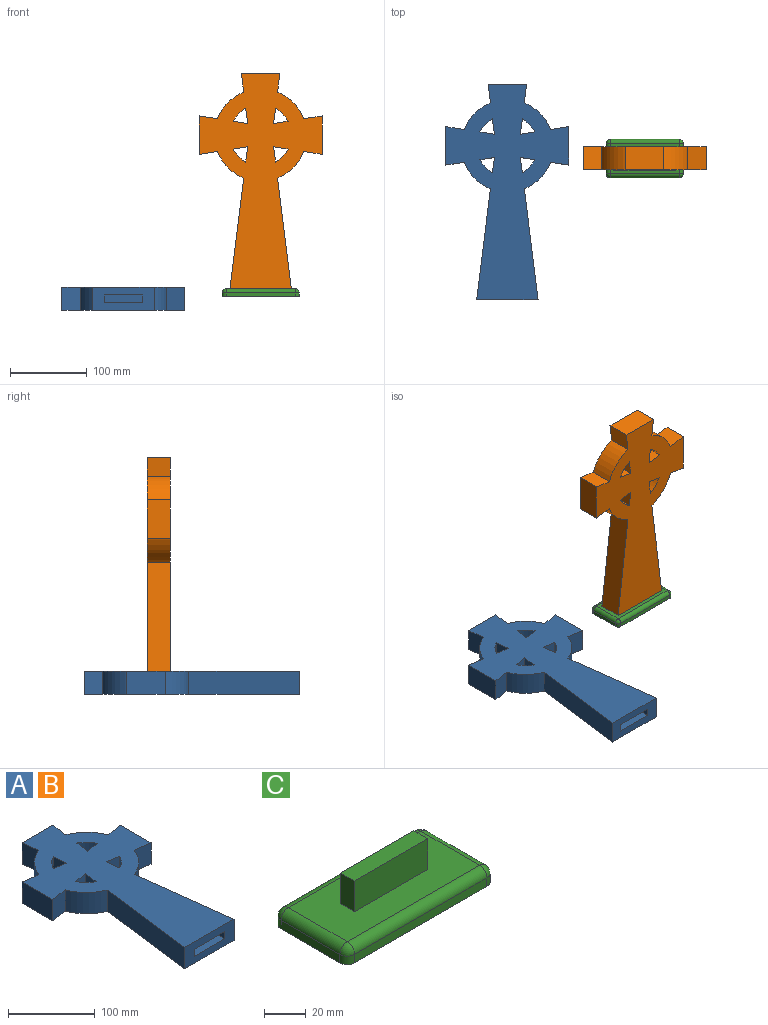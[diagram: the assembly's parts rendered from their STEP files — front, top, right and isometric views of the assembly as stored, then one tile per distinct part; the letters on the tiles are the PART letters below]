
ASSEMBLY  parts=3 mates=1
PART A: 35 faces, bbox 160x280x30 mm
  f0: plane 80x30mm, normal (0,-1,0), area 1900mm2, adj f15,f16,f28,f29,f30,f31,f32,f33
  f1: plane 30x18.79mm, normal (0.15,-0.99,0), area 570.6mm2, adj f2,f27,f28,f29
  f2: plane 30x19.86mm, normal (-0.99,0.12,0), area 600.3mm2, adj f1,f27,f28,f29
  f3: plane 30x19.86mm, normal (0.99,0.12,0), area 600.3mm2, adj f4,f23,f28,f29
  f4: plane 30x18.79mm, normal (-0.15,-0.99,0), area 570.6mm2, adj f3,f23,f28,f29
  f5: cylinder r=40mm len=30mm, axis (0,0,-1), area 715.5mm2, adj f6,f24,f28,f29
  f6: plane 30x19.86mm, normal (-0.99,-0.12,0), area 600.3mm2, adj f5,f24,f28,f29
  f7: plane 30x19.86mm, normal (0.99,-0.12,0), area 600.3mm2, adj f8,f25,f28,f29
  f8: cylinder r=40mm len=30mm, axis (0,0,-1), area 715.5mm2, adj f7,f25,f28,f29
  f9: plane 30x24.17mm, normal (-0.99,-0.12,0), area 730.8mm2, adj f10,f26,f28,f29
  f10: cylinder r=60mm len=34.56mm, axis (0,0,-1), area 1500.2mm2, adj f9,f11,f28,f29
  f11: plane 30x23.9mm, normal (0.15,0.99,0), area 725.6mm2, adj f10,f12,f28,f29
  f12: plane 50x30mm, normal (-1,0,0), area 1500mm2, adj f11,f13,f28,f29
  f13: plane 30x23.9mm, normal (0.15,-0.99,0), area 725.6mm2, adj f12,f14,f28,f29
  f14: cylinder r=60mm len=34.56mm, axis (0,0,-1), area 1500.2mm2, adj f13,f15,f28,f29
  f15: plane 144.17x30mm, normal (-0.99,0.12,0), area 4358.8mm2, adj f0,f14,f28,f29
  f16: plane 144.17x30mm, normal (0.99,0.12,0), area 4358.8mm2, adj f0,f17,f28,f29
  f17: cylinder r=60mm len=34.56mm, axis (0,0,-1), area 1500.2mm2, adj f16,f18,f28,f29
  f18: plane 30x23.9mm, normal (-0.15,-0.99,0), area 725.6mm2, adj f17,f19,f28,f29
  f19: plane 50x30mm, normal (1,0,0), area 1500mm2, adj f18,f20,f28,f29
  f20: plane 30x23.9mm, normal (-0.15,0.99,0), area 725.6mm2, adj f19,f21,f28,f29
  f21: cylinder r=60mm len=34.56mm, axis (0,0,-1), area 1500.2mm2, adj f20,f22,f28,f29
  f22: plane 30x24.17mm, normal (0.99,-0.12,0), area 730.8mm2, adj f21,f26,f28,f29
  f23: cylinder r=40mm len=30mm, axis (0,0,-1), area 715.5mm2, adj f3,f4,f28,f29
  f24: plane 30x18.79mm, normal (0.15,0.99,0), area 570.6mm2, adj f5,f6,f28,f29
  f25: plane 30x18.79mm, normal (-0.15,0.99,0), area 570.6mm2, adj f7,f8,f28,f29
  f26: plane 50x30mm, normal (0,1,0), area 1500mm2, adj f9,f22,f28,f29
  f27: cylinder r=40mm len=30mm, axis (0,0,-1), area 715.5mm2, adj f1,f2,f28,f29
  f28: plane 280x160mm, normal (0,0,1), area 22280.6mm2, adj f0,f1,f2,f3,f4,f5,f6,f7
  f29: plane 280x160mm, normal (0,0,-1), area 22280.6mm2, adj f0,f1,f2,f3,f4,f5,f6,f7
  f30: plane 50x20mm, normal (0,0,-1), area 1000mm2, adj f0,f31,f33,f34
  f31: plane 20x10mm, normal (1,0,0), area 200mm2, adj f0,f30,f32,f34
  f32: plane 50x20mm, normal (0,0,1), area 1000mm2, adj f0,f31,f33,f34
  f33: plane 20x10mm, normal (-1,0,0), area 200mm2, adj f0,f30,f32,f34
  f34: plane 50x10mm, normal (0,-1,0), area 500mm2, adj f30,f31,f32,f33
PART B: same geometry as A
PART C: 23 faces, bbox 100x50x28 mm
  f0: plane 90x40mm, normal (0,0,1), area 3112mm2, adj f6,f7,f12,f13,f17,f18,f21,f22
  f1: plane 90x5mm, normal (0,1,0), area 450mm2, adj f5,f11,f17,f20
  f2: plane 40x5mm, normal (-1,0,0), area 200mm2, adj f5,f14,f18,f20
  f3: plane 90x5mm, normal (0,-1,0), area 450mm2, adj f5,f9,f13,f14
  f4: plane 40x5mm, normal (1,0,0), area 200mm2, adj f5,f9,f11,f12
  f5: plane 100x50mm, normal (0,0,-1), area 4978.5mm2, adj f1,f2,f3,f4,f9,f11,f14,f20
  f6: plane 18x9.8mm, normal (-1,0,0), area 172.8mm2, adj f0,f8,f21,f22
  f7: plane 18x9.8mm, normal (1,0,0), area 172.8mm2, adj f0,f8,f21,f22
  f8: plane 49.8x9.4mm, normal (0,0,1), area 468.1mm2, adj f6,f7,f21,f22
  f9: cylinder r=5mm len=5mm, axis (0,0,1), area 39.3mm2, adj f3,f4,f5,f10
  f10: sphere r=5mm, area 39.3mm2, adj f9,f12,f13
  f11: cylinder r=5mm len=5mm, axis (0,0,-1), area 39.3mm2, adj f1,f4,f5,f15
  f12: cylinder r=5mm len=40mm, axis (0,-1,0), area 314.2mm2, adj f0,f4,f10,f15
  f13: cylinder r=5mm len=90mm, axis (-1,0,0), area 706.9mm2, adj f0,f3,f10,f16
  f14: cylinder r=5mm len=5mm, axis (0,0,-1), area 39.3mm2, adj f2,f3,f5,f16
  f15: sphere r=5mm, area 39.3mm2, adj f11,f12,f17
  f16: sphere r=5mm, area 39.3mm2, adj f13,f14,f18
  f17: cylinder r=5mm len=90mm, axis (1,0,0), area 706.9mm2, adj f0,f1,f15,f19
  f18: cylinder r=5mm len=40mm, axis (0,1,0), area 314.2mm2, adj f0,f2,f16,f19
  f19: sphere r=5mm, area 39.3mm2, adj f17,f18,f20
  f20: cylinder r=5mm len=5mm, axis (0,0,1), area 39.3mm2, adj f1,f2,f5,f19
  f21: plane 49.8x18mm, normal (0,1,0.01), area 896.5mm2, adj f0,f6,f7,f8
  f22: plane 49.8x18mm, normal (0,-1,0.01), area 896.5mm2, adj f0,f6,f7,f8
PLACE A t=(-121.09,21.65,-32.51)mm
PLACE B rot(axis=(1,0,0),90deg) t=(57.48,20.13,195.49)mm
PLACE C t=(-122.28,25.61,-14.55)mm
MATE slider B.f0 <-> C.f8  axis (0,0,-1) through (57.48,5.13,-4.51)mm
